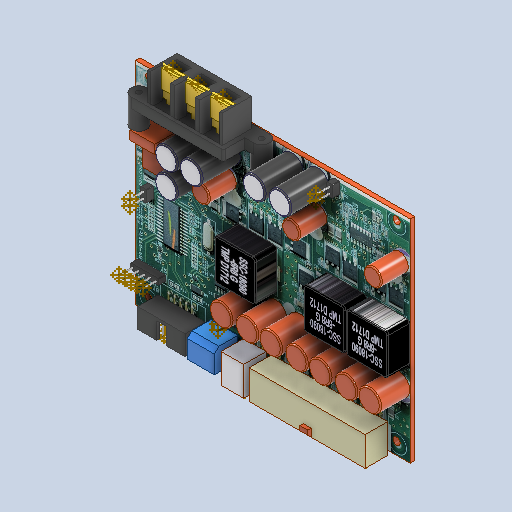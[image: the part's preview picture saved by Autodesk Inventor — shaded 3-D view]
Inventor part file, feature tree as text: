
AUTODESK INVENTOR PART (.ipt)
format: ipt  version: 2022 (Build 260153000, 153)  size: 2,741,248 bytes
history: native  units: mm
features: sketch x68, extrude x23, other x23, fillet x7, projected_geometry x6, pattern_linear x3, chamfer x2, hole x1
ambient origin geometry x8: Origin, YZ Plane, XZ Plane, XY Plane, X Axis, Y Axis, Z Axis, Center Point
bodies: Solid1 (feature_tree)
feature tree (133):
  sketch  "Sketch1"  dims[d0=122.0mm d1=94.0mm]
  extrude  "Extrusion1"  Depth=94.0mm
  hole  "Hole1"  [1 undecoded]
  sketch  "Sketch3"  dims[d2=2.0mm d3=0.0mm d4=85.0mm]
  extrude  "Extrusion3"  Depth=3.5mm
  extrude  "Extrusion4"  Depth=5.5mm
  sketch  "Sketch5"  dims[d7=6.0mm d8=5.5mm d9=3.2mm d10=6.0mm d11=6.3mm d12=2.0mm d13=90.0deg d14=8.0mm d15=0.0mm d22=2.0mm d23=13.0mm d24=51.5mm d25=10.0mm d26=0.0mm d28=28.0mm d36=13.0mm d37=0.0mm d38=10.0mm d39=10.0mm d41=10.0mm d42=10.0mm d43=10.0mm d46=17.0mm d47=0.0mm d48=10.5mm d49=11.5mm d50=10.5mm d51=11.5mm d52=10.5mm d53=11.5mm d54=10.0mm d55=5.2mm d56=18.4mm d57=21.3mm d58=37.4mm d59=0.5mm d60=39.0mm d61=2.5mm d62=9.5mm d63=0.0mm d65=1.5mm d66=0.5mm d67=10.0mm d68=10.0mm d69=2.5mm d70=12.0mm d71=10.0mm d72=2.5mm d73=2.5mm d74=1.0mm d75=21.0mm d76=9.0mm d77=0.2mm d78=10.5mm d79=0.0mm d80=9.0mm d81=0.0mm d82=3.5mm d83=1.5mm d84=0.0mm d85=1.5mm d86=2.0mm d87=45.0deg d88=2.6mm d89=0.7mm d90=2.6mm d91=12.5mm d92=2.6mm d93=2.6mm d94=2.6mm d95=0.8mm d96=15.5mm d97=5.3mm d98=44.5mm d100=1.3mm d101=2.6mm d102=1.3mm d103=2.6mm d104=1.3mm d105=2.6mm d106=1.2mm d107=31.5mm d108=16.0mm d110=76.2mm d111=75.0mm d112=3.0mm d113=0.0mm d114=9.5mm d115=0.0mm d116=0.2mm d117=2.0mm d118=2.0mm d119=45.0deg d120=1.1mm d121=1.1mm d122=0.5mm d123=0.5mm d124=1.0mm d125=9.5mm d126=0.0mm d127=9.5mm d128=0.0mm d129=120.0mm d131=4.15mm d132=21.5mm d133=36.0mm d134=0.8mm d135=8.0mm d136=14.8mm d137=0.8mm d138=44.3mm d139=21.0mm d140=21.0mm d141=64.0mm d142=12.0mm d143=0.0mm d144=30.5mm d149=37.0mm d151=52.0mm d152=16.5mm d154=7.0mm d155=2.3mm d156=11.0mm d157=3.0mm d158=0.0mm d159=11.0mm d160=0.0mm d161=1.0mm d162=33.0mm d163=13.0mm d164=1.5mm d165=2.0mm d166=9.0mm d167=10.0mm d168=6.5mm d169=2.5mm d170=1.2mm d171=4.0mm d172=14.0mm d173=0.0mm d174=14.0mm d175=0.0mm d176=30.0mm d178=11.0mm d179=5.0mm d180=12.5mm d181=0.0mm d182=21.5mm d183=0.0mm d184=0.5mm d185=0.5mm d186=1.0mm d187=0.0mm d188=30.0mm d190=11.0mm d191=13.0mm d192=11.0mm d193=4.0mm d194=1.0mm d195=11.5mm d198=0.0mm d199=0.0mm d200=1.5mm d201=9.0mm d202=0.0mm d203=15.0mm d204=0.0mm d205=13.0mm d206=1.0mm d207=0.5mm d208=0.5mm d209=1.4mm d210=1.4mm d211=1.4mm d212=1.4mm d213=4.2mm d214=0.8mm d215=2.5mm d216=2.5mm d217=7.5mm d218=0.0mm]
  extrude  "Extrusion5"  Depth=2.0mm
  extrude  "Выдавливание6"  Depth=13.0mm
  fillet  "Сопряжение2"  Radius=51.5mm
  extrude  "Выдавливание7"  Depth=10.0mm TaperAngle=0.0deg
  extrude  "Выдавливание8"  Depth=28.0mm
  extrude  "Выдавливание9"  Depth=13.0mm TaperAngle=0.0deg
  chamfer  "Фаска1"  Distance=10.0mm
  sketch  "Эскиз8"
  extrude  "Выдавливание10"  Depth=10.0mm
  extrude  "Выдавливание11"  Depth=10.0mm
  fillet  "Сопряжение4"  Radius=10.0mm
  chamfer  "Фаска2"  Distance=10.0mm
  sketch  "Эскиз9"
  extrude  "Выдавливание12"  Depth=17.0mm TaperAngle=0.0deg
  extrude  "Выдавливание13"  Depth=10.5mm
  pattern_linear  "Прямоуг.массив1"  Spacing1=11.5mm  [1 undecoded]
  extrude  "Выдавливание14"  Depth=10.5mm
  fillet  "Сопряжение3"  Radius=11.5mm
  sketch  "Эскиз10"
  extrude  "Выдавливание15"  Depth=10.5mm
  extrude  "Выдавливание16"  Depth=11.5mm
  other  "Непосредственное редактирование1"
  fillet  "Сопряжение5"  Radius=10.0mm
  sketch  "Эскиз11"
  extrude  "Выдавливание17"  Depth=5.2mm
  extrude  "Выдавливание18"  Depth=18.4mm
  pattern_linear  "Прямоуг.массив2"  Spacing1=21.3mm  [1 undecoded]
  sketch  "Эскиз12"
  extrude  "Выдавливание19"  Depth=37.4mm
  extrude  "Выдавливание20"  Depth=0.5mm
  extrude  "Выдавливание21"  Depth=39.0mm
  pattern_linear  "Прямоуг.массив3"  Spacing1=2.5mm  [1 undecoded]
  sketch  "Эскиз14"
  extrude  "Выдавливание22"  Depth=9.5mm TaperAngle=0.0deg
  extrude  "Выдавливание23"  Depth=1.5mm
  fillet  "Сопряжение6"  Radius=0.5mm
  fillet  "Сопряжение7"  Radius=10.0mm
  fillet  "Сопряжение8"  Radius=10.0mm
  extrude  "Выдавливание24"  Depth=2.5mm
  sketch  "Эскиз16"
  other  "Маркировка2"
  other  "Маркировка3"
  other  "Маркировка4"
  other  "Маркировка5"
  sketch  "Эскиз22"
  sketch  "Эскиз23"
  sketch  "Эскиз24"
  sketch  "Эскиз25"
  sketch  "Эскиз26"
  sketch  "Эскиз27"
  sketch  "Эскиз28"
  sketch  "Эскиз29"
  sketch  "Эскиз30"
  sketch  "Эскиз31"
  sketch  "Эскиз32"
  sketch  "Эскиз33"
  sketch  "Эскиз34"
  sketch  "Эскиз35"
  sketch  "Эскиз36"
  sketch  "Эскиз37"
  sketch  "Эскиз38"
  sketch  "Эскиз39"
  sketch  "Эскиз40"
  sketch  "Эскиз41"
  sketch  "Эскиз42"
  sketch  "Эскиз43"
  sketch  "Эскиз44"
  sketch  "Эскиз45"
  sketch  "Эскиз46"
  sketch  "Эскиз47"
  sketch  "Эскиз48"
  sketch  "Эскиз49"
  sketch  "Эскиз50"
  sketch  "Эскиз51"
  sketch  "Эскиз52"
  sketch  "Эскиз53"
  sketch  "Эскиз54"
  sketch  "Эскиз55"
  sketch  "Эскиз56"
  sketch  "Эскиз57"
  sketch  "Эскиз58"
  sketch  "Эскиз59"
  sketch  "Эскиз60"
  sketch  "Эскиз61"
  sketch  "Эскиз62"
  sketch  "Эскиз63"
  sketch  "Эскиз64"
  sketch  "Эскиз65"
  sketch  "Эскиз66"
  sketch  "Эскиз67"
  sketch  "Эскиз68"
  sketch  "Эскиз69"
  sketch  "Эскиз70"
  other  "Маркировка6"
  sketch  "Sketch4"  dims[d5=110.0mm d6=3.5mm]
  sketch  "Эскиз6"
  other  "Твердое тело2"
  other  "Твердое тело3"
  other  "Твердое тело4"
  other  "Твердое тело5"
  sketch  "Эскиз7"
  other  "Твердое тело7"
  other  "Твердое тело8"
  projected_geometry  "Спроецированная петля1"
  projected_geometry  "Спроецированная петля2"
  other  "Твердое тело9"
  other  "Твердое тело10"
  other  "Твердое тело13"
  sketch  "Эскиз13"
  other  "Твердое тело14"
  other  "Твердое тело15"
  sketch  "Эскиз15"
  sketch  "Эскиз17"
  other  "Картинка4"
  projected_geometry  "Спроецированная петля3"
  sketch  "Эскиз18"
  projected_geometry  "Спроецированная петля4"
  other  "Картинка5"
  sketch  "Эскиз19"
  projected_geometry  "Спроецированная петля5"
  other  "Картинка6"
  sketch  "Эскиз21"
  other  "Картинка10"
  projected_geometry  "Спроецированная петля7"
  other  "Картинка11"
  other  "Перенос1"
note: 4 required parameter values undecoded (feature->parameter linkage not recoverable at this tier; creation-order binding heuristic only, values carry confidence <= 0.55)
